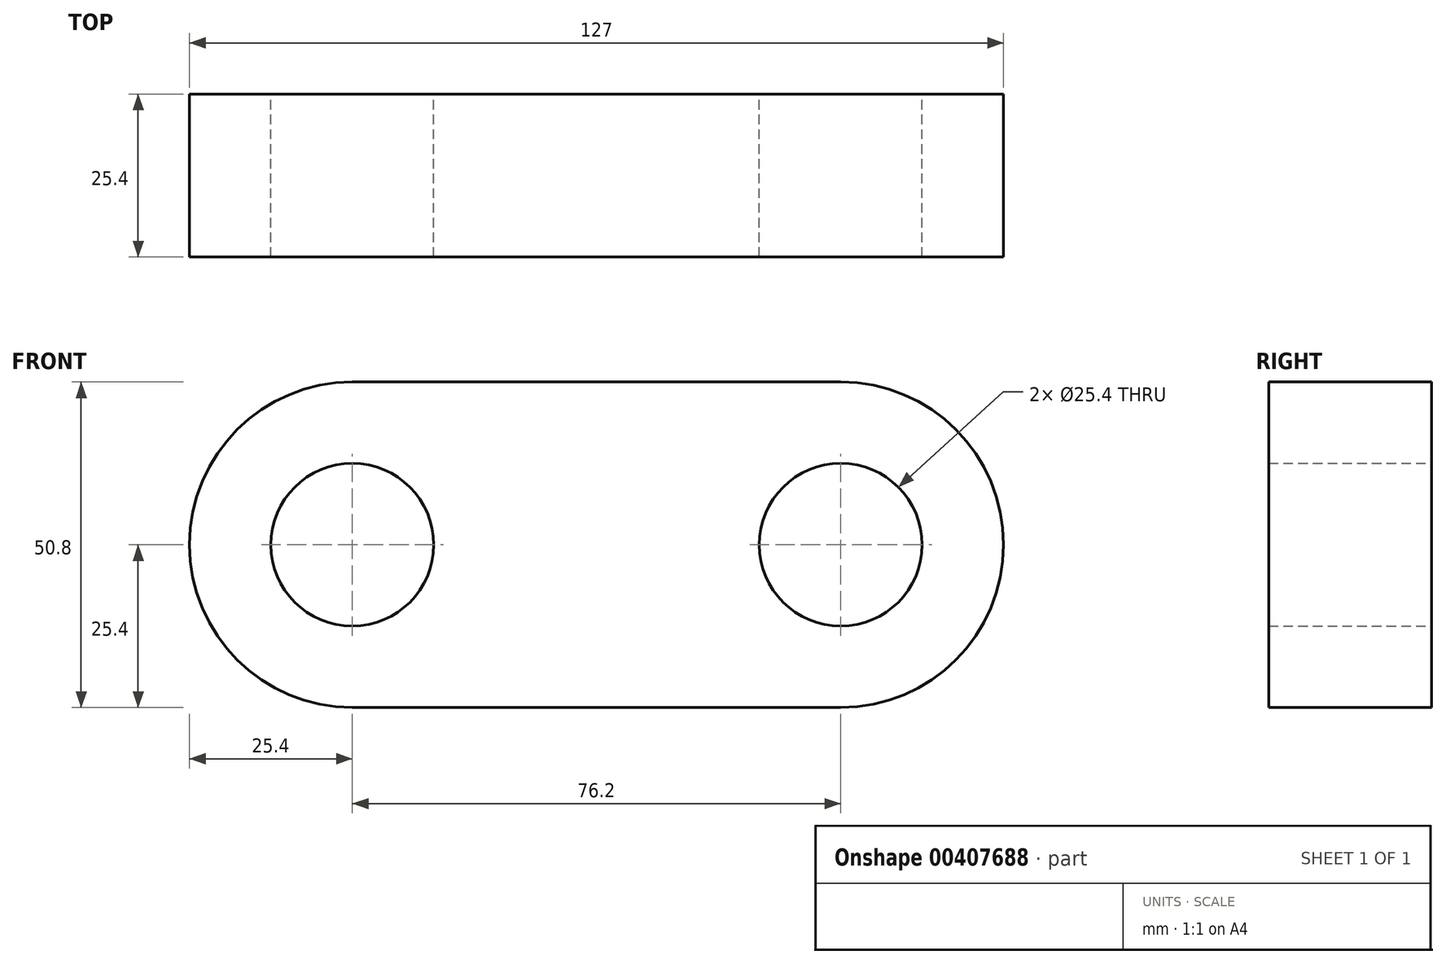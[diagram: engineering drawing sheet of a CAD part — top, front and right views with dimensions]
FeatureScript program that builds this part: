
annotation { "Feature Type Name" : "Feature", "Feature Type Description" : "" }
export const myFeature = defineFeature(function(context is Context, id is Id, definition is map)
    precondition{}
    {
        {
            var Q0;
            Q0=qCreatedBy(makeId("Front.planeOp"),FACE);
            var sketch = newSketch(context, id + "F0", { "sketchPlane" : qUnion([Q0])});
            skCircle(sketch, "E0", {"center": v(0, 0) * mm, "radius": 25.4 * mm});
            skCircle(sketch, "E1", {"center": v(76.2, 0) * mm, "radius": 25.4 * mm});
            skLineSegment(sketch, "E2", {"start": v(0, 25.4) * mm, "end": v(76.2, 25.4) * mm});
            skLineSegment(sketch, "E3", {"start": v(0, -25.4) * mm, "end": v(76.2, -25.4) * mm});
            skCircle(sketch, "E4", {"center": v(0, 0) * mm, "radius": 12.7 * mm});
            skCircle(sketch, "E5", {"center": v(76.2, 0) * mm, "radius": 12.7 * mm});
            skSolve(sketch);
        }
        {
            var Q0;
            Q0 = qSketchRegion(id + "F0", true);
            extrude(context, id + "F1", {"entities" : qUnion([Q0]), "depth" : 25.4 * mm});
        }
    });
